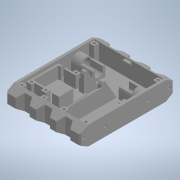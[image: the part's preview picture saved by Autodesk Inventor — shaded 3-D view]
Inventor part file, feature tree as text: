
AUTODESK INVENTOR PART (.ipt)
format: ipt  version: 2020 (Build 240168000, 168)  size: 1,050,112 bytes
history: native  units: in
note: dims shown in document units (in); Inventor stores cm internally (conversion verified against a paired STEP export)
features: projected_geometry x34, extrude x21, sketch x21, mirror x6, plane x1, chamfer x1
ambient origin geometry x8: Origin, YZ Plane, XZ Plane, XY Plane, X Axis, Y Axis, Z Axis, Center Point
bodies: Solid1 (feature_tree)
feature tree (84):
  extrude  "Extrusion1"  Depth=5.9055in
  extrude  "Extrusion2"  TaperAngle=0.0deg  [1 undecoded]
  extrude  "Extrusion3"  Depth=1.063in
  extrude  "Extrusion4"  Depth=0.315in
  extrude  "Extrusion5"  TaperAngle=0.0deg  [1 undecoded]
  extrude  "Extrusion6"  Depth=0.5906in
  mirror  "Mirror1"
  extrude  "Extrusion7"  Depth=0.0787in
  mirror  "Mirror2"
  extrude  "Extrusion8"  Depth=0.6102in
  mirror  "Mirror3"
  plane  "Work Plane1"
  extrude  "Extrusion9"  Depth=0.7874in TaperAngle=0.0deg
  mirror  "Mirror4"
  extrude  "Extrusion10"  Depth=6.063in TaperAngle=0.0deg
  extrude  "Extrusion11"  Depth=0.1575in
  sketch  "Sketch20"  dims[d27=1.5748in d28=0.0in d29=0.0in]
  extrude  "Extrusion17"  TaperAngle=0.0deg  [1 undecoded]
  extrude  "Extrusion19"  Depth=0.2756in
  mirror  "Mirror7"
  extrude  "Extrusion20"  Depth=0.4331in
  extrude  "Extrusion22"  Depth=2.7559in
  extrude  "Extrusion25"  Depth=0.0453in
  extrude  "Extrusion26"  TaperAngle=0.0deg  [1 undecoded]
  extrude  "Extrusion27"  Depth=0.0787in
  extrude  "Extrusion28"  Depth=0.993in
  extrude  "Extrusion29"  Depth=0.2756in
  sketch  "Sketch32"  dims[d46=0.315in d48=0.993in]
  extrude  "Extrusion30"  Depth=0.4724in
  mirror  "Mirror9"
  chamfer  "Chamfer1"  Distance=1.5748in
  sketch  "Sketch39"  dims[d54=0.0in d55=0.4724in d57=1.5748in d58=1.6142in d59=0.1181in d60=0.1969in d89=0.0157in d90=0.0157in d91=0.1476in d92=0.1476in d96=0.315in d97=0.1575in d98=0.1181in d99=0.0in d108=0.0394in d109=0.0in d110=0.063in d111=0.0394in d112=0.0in d121=45.0deg d122=0.993in d123=0.1969in d124=0.3937in d125=0.0in d134=0.3346in d135=0.1772in d138=0.2362in d139=0.3937in d140=0.1969in d141=0.5388in d142=0.1181in d143=1.1024in d144=0.8661in d145=0.0in d146=0.1181in d149=0.315in d151=0.1181in d152=0.0in d153=0.1181in d154=0.0in d155=0.1476in d156=0.2756in d157=0.0in d158=0.5906in d160=0.993in d161=0.1969in d162=45.0deg d163=0.3937in d164=0.0in d168=0.1575in d184=0.1965in d185=0.0in d186=0.0787in d187=0.0787in d188=45.0deg d204=1.5748in d206=1.2761in d207=0.3937in d209=0.3937in d211=0.5118in d213=0.5766in]
  sketch  "Sketch1"  dims[d0=1.1811in d1=5.9055in]
  sketch  "Sketch2"  dims[d2=4.6457in d3=0.0in]
  projected_geometry  "Projected Loop1"
  sketch  "Sketch3"  dims[d4=0.1575in d5=1.063in]
  projected_geometry  "Projected Loop2"
  projected_geometry  "Projected Loop3"
  sketch  "Sketch4"  dims[d6=0.0in d8=0.315in]
  sketch  "Sketch5"  dims[d10=0.993in d11=0.0in]
  projected_geometry  "Projected Loop4"
  sketch  "Sketch6"  dims[d12=0.6496in d13=0.5906in]
  sketch  "Sketch7"  dims[d14=1.5748in d15=0.0787in]
  sketch  "Sketch9"  dims[d16=0.5512in d17=0.0in d18=0.6102in]
  sketch  "Sketch10"  dims[d19=0.4803in d20=0.7874in d21=0.0in]
  sketch  "Sketch12"  dims[d22=0.1654in d23=6.063in d24=0.0in]
  projected_geometry  "Projected Loop6"
  projected_geometry  "Projected Loop7"
  projected_geometry  "Projected Loop8"
  sketch  "Sketch13"  dims[d25=0.5114in d26=0.1575in]
  projected_geometry  "Projected Loop19"
  projected_geometry  "Projected Loop20"
  projected_geometry  "Projected Loop21"
  projected_geometry  "Projected Loop22"
  projected_geometry  "Projected Loop23"
  projected_geometry  "Projected Loop24"
  sketch  "Sketch22"  dims[d30=0.1575in d31=0.2756in]
  sketch  "Sketch23"  dims[d32=0.0in d33=0.4331in]
  sketch  "Sketch26"  dims[d34=0.0906in d38=2.7559in]
  projected_geometry  "Projected Loop25"
  sketch  "Sketch29"  dims[d40=0.0453in d41=0.0909in]
  projected_geometry  "Projected Loop27"
  sketch  "Sketch30"  dims[d42=0.2362in d43=0.0in]
  projected_geometry  "Projected Loop28"
  sketch  "Sketch31"  dims[d44=60.0deg d45=0.0787in]
  projected_geometry  "Projected Loop29"
  sketch  "Sketch33"  dims[d49=0.0in d53=0.2756in]
  projected_geometry  "Projected Loop30"
  projected_geometry  "Projected Loop46"
  projected_geometry  "Projected Loop47"
  projected_geometry  "Projected Loop48"
  projected_geometry  "Projected Loop49"
  projected_geometry  "Projected Loop50"
  projected_geometry  "Projected Loop51"
  projected_geometry  "Projected Loop52"
  projected_geometry  "Projected Loop53"
  projected_geometry  "Projected Loop54"
  projected_geometry  "Projected Loop55"
  projected_geometry  "Projected Loop56"
  projected_geometry  "Projected Loop57"
  projected_geometry  "Projected Loop58"
  projected_geometry  "Projected Loop59"
  projected_geometry  "Project Cut Edges1"
  projected_geometry  "Project Cut Edges2"
note: 4 required parameter values undecoded (feature->parameter linkage not recoverable at this tier; creation-order binding heuristic only, values carry confidence <= 0.55)
